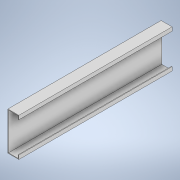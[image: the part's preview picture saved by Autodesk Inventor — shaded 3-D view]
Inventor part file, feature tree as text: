
AUTODESK INVENTOR PART (.ipt)
format: ipt  version: 2020 (Build 240168000, 168)  size: 112,640 bytes
history: native  units: mm
features: extrude x1, sketch x1
ambient origin geometry x8: Origin, YZ Plane, XZ Plane, XY Plane, X Axis, Y Axis, Z Axis, Center Point
bodies: Solid1 (feature_tree)
feature tree (2):
  extrude  "Extrusion1"  Depth=150.0mm
  sketch  "Sketch1"  dims[d0=43.0mm d1=150.0mm d2=15.0mm d3=15.0mm d4=2.5mm d5=600.0mm d6=0.0mm]
